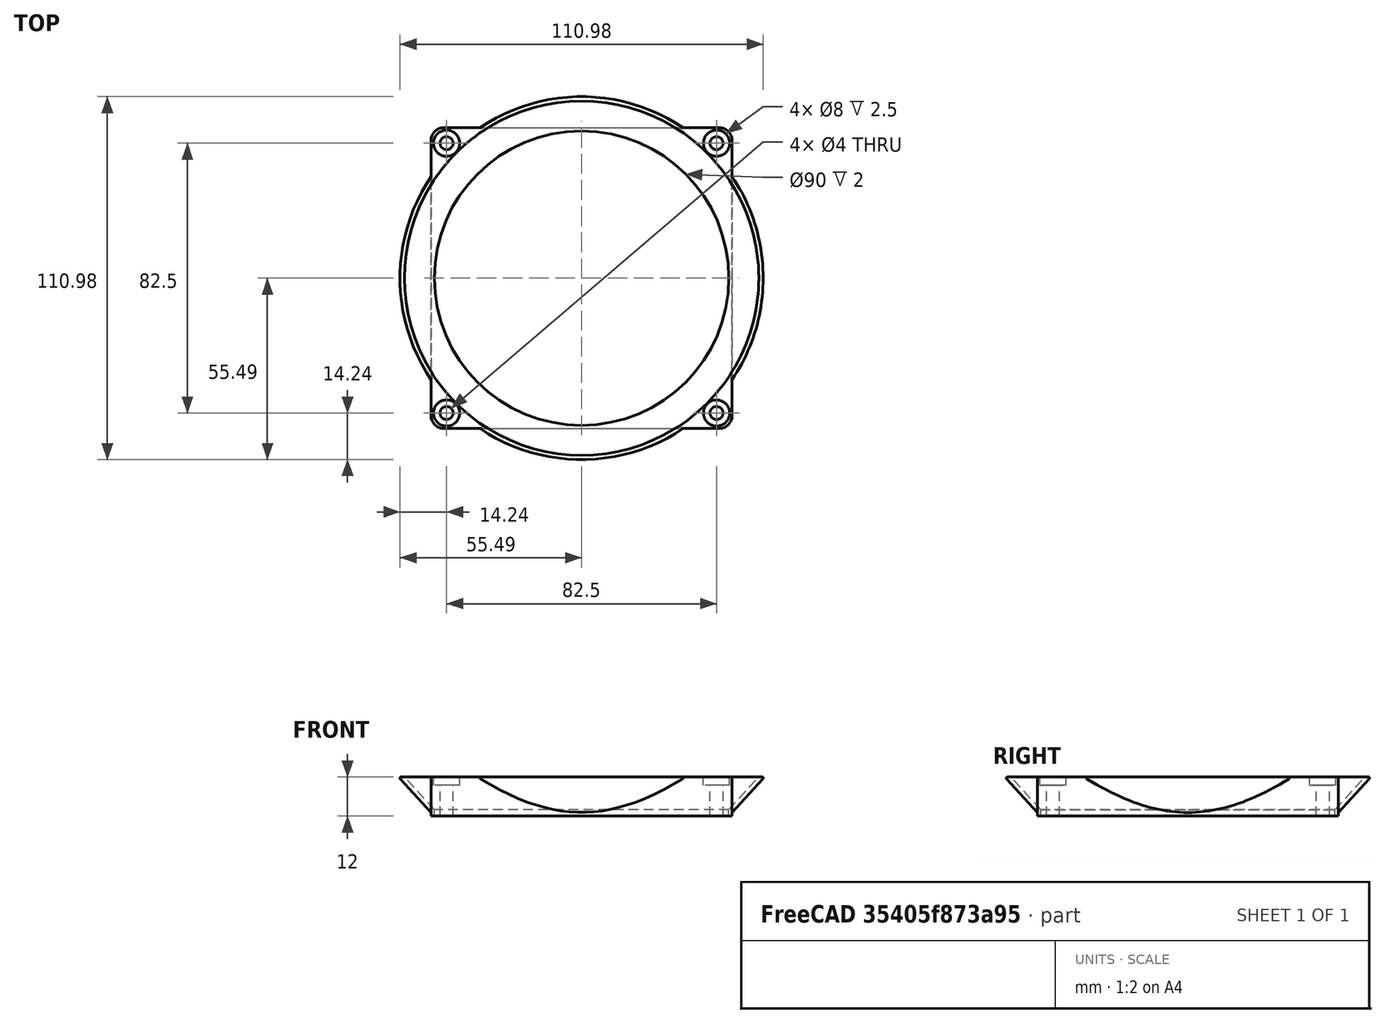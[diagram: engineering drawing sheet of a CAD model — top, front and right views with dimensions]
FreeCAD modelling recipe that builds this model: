
FCSTD DOCUMENT  (FreeCAD 0.18R16117 (Git))
Label: fan duct v3
License: All rights reserved
LicenseURL: http://en.wikipedia.org/wiki/All_rights_reserved
objects: Part::Cylinder×9, Part::MultiFuse×4, Part::Cut×3, Part::Cone×2, Part::Fillet×2, Part::Box×1
note: 21 computed .brp shape members not serialized (recipe doc carries the construction recipe); baked Part::Feature solids carry a one-line shape summary decoded from their .brp

FEATURE [Part::Box] Box  label="Cube"
  AttacherType = Attacher::AttachEngine3D
  Height = 12
  Length = 92
  Placement = pos=(-46,-46,0) rot=(0,0,1;0rad)
  Width = 92
FEATURE [Part::Cone] Cone
  Angle = 360
  AttacherType = Attacher::AttachEngine3D
  Height = 12
  Radius1 = 45
  Radius2 = 56
FEATURE [Part::Cone] Cone001
  Angle = 360
  AttacherType = Attacher::AttachEngine3D
  Height = 12
  Placement = pos=(0,0,2) rot=(0,0,1;0rad)
  Radius1 = 45
  Radius2 = 56
FEATURE [Part::Cylinder] Cylinder
  Angle = 360
  AttacherType = Attacher::AttachEngine3D
  Height = 12
  Radius = 45
FEATURE [Part::MultiFuse] Fusion
  Shapes = -> [Cylinder,Cone001]
FEATURE [Part::Fillet] Fillet
  Base = -> Cone
  Edges = 1 edges r=0.4: [Edge1]
FEATURE [Part::Fillet] Fillet001
  Base = -> Box
  Edges = 4 edges r=4: [Edge1,Edge3,Edge5,Edge7]
FEATURE [Part::MultiFuse] Fusion001
  Shapes = -> [Fillet001,Fillet]
FEATURE [Part::Cut] Cut
  Base = -> Fusion001
  Tool = -> Fusion
FEATURE [Part::Cylinder] Cylinder001
  Angle = 360
  AttacherType = Attacher::AttachEngine3D
  Height = 10
  Placement = pos=(-41.25,41.25,0) rot=(0,0,1;0rad)
  Radius = 4
FEATURE [Part::Cylinder] Cylinder002
  Angle = 360
  AttacherType = Attacher::AttachEngine3D
  Height = 10
  Placement = pos=(41.25,-41.25,0) rot=(0,0,1;0rad)
  Radius = 4
FEATURE [Part::Cylinder] Cylinder003
  Angle = 360
  AttacherType = Attacher::AttachEngine3D
  Height = 10
  Placement = pos=(-41.25,-41.25,0) rot=(0,0,1;0rad)
  Radius = 4
FEATURE [Part::Cylinder] Cylinder004
  Angle = 360
  AttacherType = Attacher::AttachEngine3D
  Height = 10
  Placement = pos=(41.25,41.25,0) rot=(0,0,1;0rad)
  Radius = 4
FEATURE [Part::MultiFuse] Fusion002
  Placement = pos=(0,0,9.5) rot=(0,0,1;0rad)
  Shapes = -> [Cylinder001,Cylinder004,Cylinder002,Cylinder003]
FEATURE [Part::Cut] Cut001
  Base = -> Cut
  Tool = -> Fusion002
FEATURE [Part::Cylinder] Cylinder005
  Angle = 360
  AttacherType = Attacher::AttachEngine3D
  Height = 11
  Placement = pos=(-41.25,41.25,0) rot=(0,0,1;0rad)
  Radius = 2
FEATURE [Part::Cylinder] Cylinder006
  Angle = 360
  AttacherType = Attacher::AttachEngine3D
  Height = 11
  Placement = pos=(41.25,41.25,0) rot=(0,0,1;0rad)
  Radius = 2
FEATURE [Part::Cylinder] Cylinder007
  Angle = 360
  AttacherType = Attacher::AttachEngine3D
  Height = 11
  Placement = pos=(41.25,-41.25,0) rot=(0,0,1;0rad)
  Radius = 2
FEATURE [Part::Cylinder] Cylinder008
  Angle = 360
  AttacherType = Attacher::AttachEngine3D
  Height = 11
  Placement = pos=(-41.25,-41.25,0) rot=(0,0,1;0rad)
  Radius = 2
FEATURE [Part::MultiFuse] Fusion003
  Shapes = -> [Cylinder005,Cylinder006,Cylinder007,Cylinder008]
FEATURE [Part::Cut] Cut002
  Base = -> Cut001
  Tool = -> Fusion003
